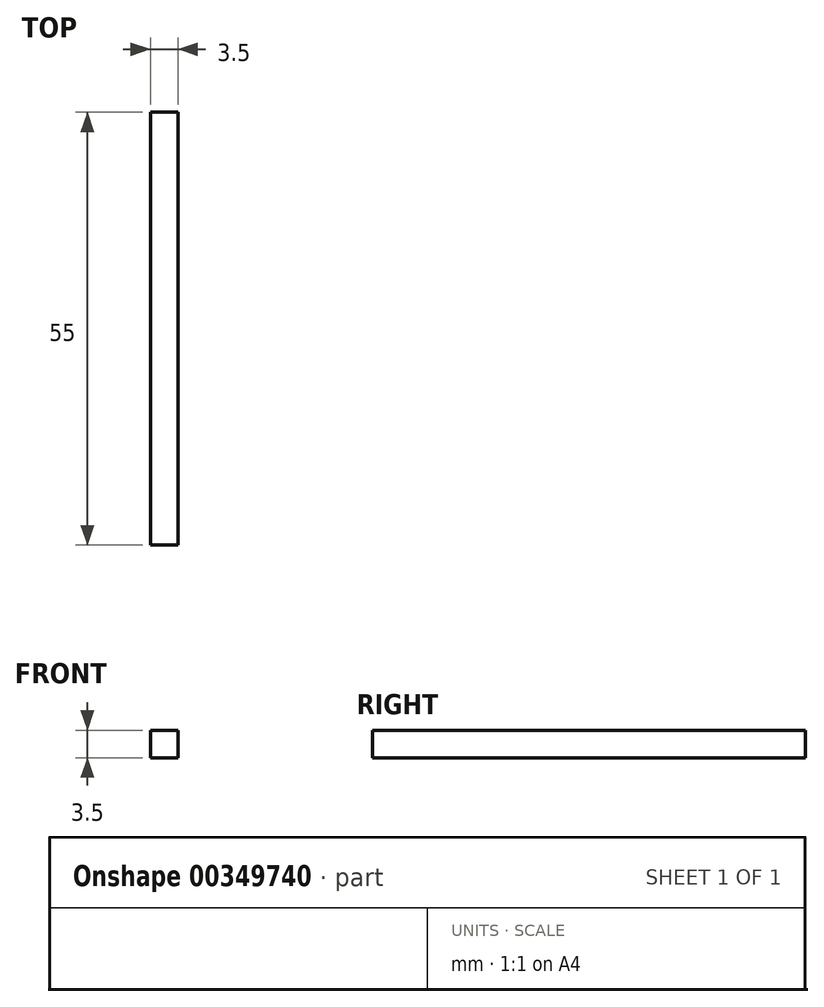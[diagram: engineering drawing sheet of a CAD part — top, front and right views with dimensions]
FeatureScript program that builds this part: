
annotation { "Feature Type Name" : "Feature", "Feature Type Description" : "" }
export const myFeature = defineFeature(function(context is Context, id is Id, definition is map)
    precondition{}
    {
        {
            var Q0;
            Q0=qCreatedBy(makeId("Top.planeOp"),FACE);
            var sketch = newSketch(context, id + "F0", { "sketchPlane" : qUnion([Q0])});
            skLineSegment(sketch, "E0.bottom", {"start": v(1.75, 27.5) * mm, "end": v(-1.75, 27.5) * mm});
            skLineSegment(sketch, "E0.top", {"start": v(1.75, -27.5) * mm, "end": v(-1.75, -27.5) * mm});
            skLineSegment(sketch, "E0.left", {"start": v(1.75, 27.5) * mm, "end": v(1.75, -27.5) * mm});
            skLineSegment(sketch, "E0.right", {"start": v(-1.75, 27.5) * mm, "end": v(-1.75, -27.5) * mm});
            skPoint(sketch, "E0.middle", {"position": v(0, 0) * mm});
            skSolve(sketch);
        }
        {
            var Q0;
            Q0=qSketchRegion(id+"F0",true);
            extrude(context, id + "F1", {"entities" : qUnion([Q0]), "depth" : 3.5 * mm});
        }
    });
